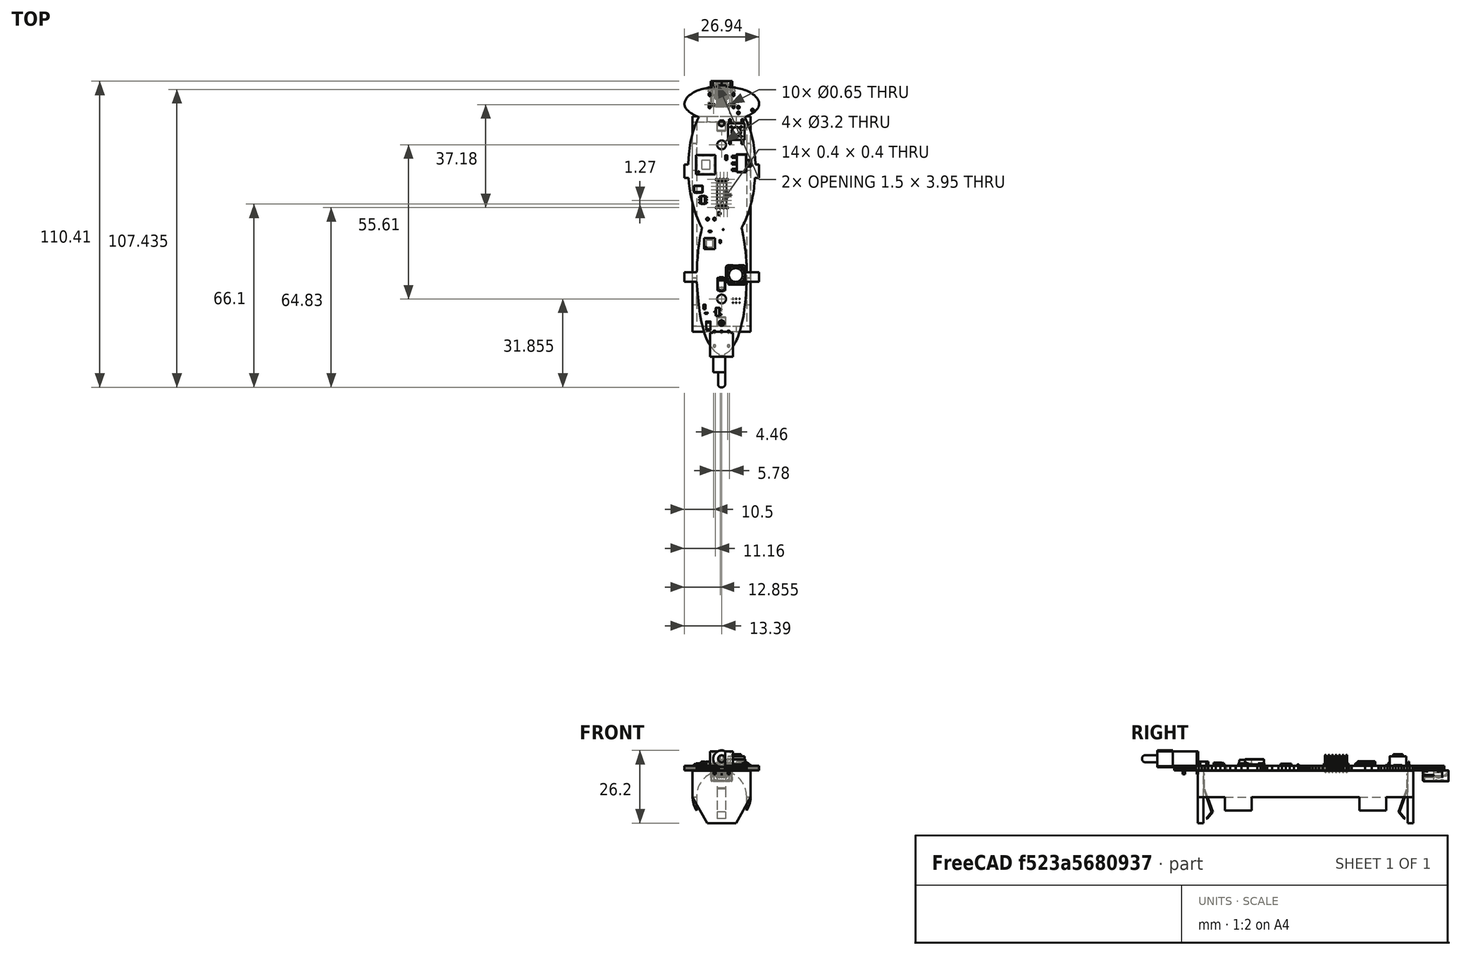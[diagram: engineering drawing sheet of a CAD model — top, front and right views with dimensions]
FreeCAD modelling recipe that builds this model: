
FCSTD DOCUMENT  (FreeCAD 0.21R30454 (Git))
Label: centerWing
License: All rights reserved
LicenseURL: http://en.wikipedia.org/wiki/All_rights_reserved
objects: App::Link×64, Part::Feature×20, App::Part×5, PartDesign::CoordinateSystem×1, Sketcher::SketchObject×1
note: 22 computed .brp shape members not serialized (recipe doc carries the construction recipe); baked Part::Feature solids carry a one-line shape summary decoded from their .brp

FEATURE [PartDesign::CoordinateSystem] Local_CS_931
  AttacherType = Attacher::AttachEngine3D
  MapMode = 2
  Support = -> [X_Axis001]
FEATURE [Part::Feature] Pcb_931
  shape: bbox 26.94 x 97.45 x 1.6 mm, 316 faces (baked)
FEATURE [Sketcher::SketchObject] PCB_Sketch_931
  FullyConstrained = false
  sketch-geometry (258):
    g0: LineSegment StartX=204.611 StartY=-59.7706 StartZ=0 EndX=204.161 EndY=-58.747 EndZ=0
    g1: LineSegment StartX=207.307 StartY=-79.6422 StartZ=0 EndX=208.849 EndY=-79.6422 EndZ=0
    g2: LineSegment StartX=203.133 StartY=-100.504 StartZ=0 EndX=202.842 EndY=-99.0355 EndZ=0
    g3: LineSegment StartX=198.204 StartY=-141.964 StartZ=0 EndX=198.335 EndY=-141.829 EndZ=0
    g4: LineSegment StartX=196.821 StartY=-46.2543 StartZ=0 EndX=195.381 EndY=-46.2543 EndZ=0
    g5: LineSegment StartX=186.994 StartY=-104.828 StartZ=0 EndX=186.849 EndY=-106.147 EndZ=0
    g6: LineSegment StartX=190.699 StartY=-139.374 StartZ=0 EndX=191.002 EndY=-139.905 EndZ=0
    g7: LineSegment StartX=194.282 StartY=-143.161 StartZ=0 EndX=194.282 EndY=-143.702 EndZ=0
    g8: LineSegment StartX=206.155 StartY=-49.1673 StartZ=0 EndX=205.642 EndY=-48.8567 EndZ=0
    g9: LineSegment StartX=207.546 StartY=-55.4632 StartZ=0 EndX=207.833 EndY=-55.1801 EndZ=0
    g10: LineSegment StartX=191.879 StartY=-141.193 StartZ=0 EndX=192.157 EndY=-141.532 EndZ=0
    g11: LineSegment StartX=186.361 StartY=-117.075 StartZ=0 EndX=186.651 EndY=-121.509 EndZ=0
    g12: LineSegment StartX=208.789 StartY=-53.5041 StartZ=0 EndX=208.834 EndY=-53.2317 EndZ=0
    g13: LineSegment StartX=206.019 StartY=-88.581 StartZ=0 EndX=206.204 EndY=-87.8001 EndZ=0
    g14: LineSegment StartX=203.931 StartY=-123.5 StartZ=0 EndX=204.11 EndY=-121.509 EndZ=0
    g15: LineSegment StartX=183.585 StartY=-81.6183 StartZ=0 EndX=183.791 EndY=-83.5056 EndZ=0
    g16: LineSegment StartX=201.902 StartY=-134.849 StartZ=0 EndX=202.197 EndY=-133.815 EndZ=0
    g17: LineSegment StartX=202.746 StartY=-97.2753 StartZ=0 EndX=202.978 EndY=-96.8717 EndZ=0
    g18: LineSegment StartX=202.76 StartY=-131.45 StartZ=0 EndX=203.025 EndY=-130.106 EndZ=0
    g19: LineSegment StartX=184.261 StartY=-65.7953 StartZ=0 EndX=184.058 EndY=-66.826 EndZ=0
    g20: LineSegment StartX=202.505 StartY=-97.6016 StartZ=0 EndX=202.585 EndY=-97.5204 EndZ=0
    g21: LineSegment StartX=196.48 StartY=-143.161 StartZ=0 EndX=196.623 EndY=-143.098 EndZ=0
    g22: LineSegment StartX=185.289 StartY=-56.8742 StartZ=0 EndX=185.841 EndY=-57.153 EndZ=0
    g23: LineSegment StartX=208.834 StartY=-53.2317 StartZ=0 EndX=208.851 EndY=-52.9624 EndZ=0
    g24: LineSegment StartX=204.4 StartY=-117.075 StartZ=0 EndX=208.849 EndY=-117.075 EndZ=0
    g25: LineSegment StartX=185.651 StartY=-48.576 StartZ=0 EndX=185.119 EndY=-48.8567 EndZ=0
    g26: LineSegment StartX=200.369 StartY=-138.788 StartZ=0 EndX=200.678 EndY=-138.143 EndZ=0
    g27: LineSegment StartX=185.964 StartY=-92.6642 StartZ=0 EndX=186.78 EndY=-94.7637 EndZ=0
    g28: LineSegment StartX=198.468 StartY=-141.686 StartZ=0 EndX=198.604 EndY=-141.532 EndZ=0
    g29: LineSegment StartX=200.262 StartY=-47.1518 StartZ=0 EndX=199.594 EndY=-47.0453 EndZ=0
    g30: LineSegment StartX=186.393 StartY=-112.527 StartZ=0 EndX=186.377 EndY=-113.724 EndZ=0
    g31: LineSegment StartX=182.209 StartY=-51.6716 StartZ=0 EndX=182.103 EndY=-51.9211 EndZ=0
    g32: LineSegment StartX=187.169 StartY=-103.429 StartZ=0 EndX=186.994 EndY=-104.828 EndZ=0
    g33: LineSegment StartX=197.156 StartY=-142.81 StartZ=0 EndX=197.366 EndY=-142.672 EndZ=0
    g34: LineSegment StartX=203.992 StartY=-48.0954 StartZ=0 EndX=203.408 EndY=-47.8915 EndZ=0
    g35: LineSegment StartX=200.678 StartY=-138.143 StartZ=0 EndX=200.987 EndY=-137.433 EndZ=0
    g36: LineSegment StartX=191.301 StartY=-140.383 StartZ=0 EndX=191.593 EndY=-140.811 EndZ=0
    g37: LineSegment StartX=186.503 StartY=-110.129 StartZ=0 EndX=186.46 EndY=-110.807 EndZ=0
    g38: LineSegment StartX=183.377 StartY=-72.3896 StartZ=0 EndX=183.215 EndY=-74.8986 EndZ=0
    g39: LineSegment StartX=206.647 StartY=-49.5098 StartZ=0 EndX=206.155 EndY=-49.1673 EndZ=0
    g40: LineSegment StartX=201.601 StartY=-135.792 StartZ=0 EndX=201.902 EndY=-134.849 EndZ=0
    g41: LineSegment StartX=203.408 StartY=-47.8915 StartZ=0 EndX=202.807 EndY=-47.709 EndZ=0
    g42: LineSegment StartX=208.428 StartY=-51.4271 StartZ=0 EndX=208.284 EndY=-51.188 EndZ=0
    g43: LineSegment StartX=182.294 StartY=-54.3351 StartZ=0 EndX=182.469 EndY=-54.6157 EndZ=0
    g44: LineSegment StartX=185.119 StartY=-48.8567 StartZ=0 EndX=184.607 EndY=-49.1673 EndZ=0
    g45: LineSegment StartX=204.382 StartY=-93.7798 StartZ=0 EndX=204.798 EndY=-92.6642 EndZ=0
    g46: LineSegment StartX=183.215 StartY=-74.8986 StartZ=0 EndX=181.912 EndY=-74.8986 EndZ=0
    g47: LineSegment StartX=205.216 StartY=-91.4223 StartZ=0 EndX=205.627 EndY=-90.0595 EndZ=0
    g48: LineSegment StartX=208.849 StartY=-74.8986 StartZ=0 EndX=207.546 EndY=-74.8986 EndZ=0
    g49: LineSegment StartX=186.651 StartY=-121.509 StartZ=0 EndX=187.031 EndY=-125.349 EndZ=0
    g50: LineSegment StartX=204.125 StartY=-108.431 StartZ=0 EndX=203.913 EndY=-106.147 EndZ=0
    g51: LineSegment StartX=187.38 StartY=-101.978 StartZ=0 EndX=187.169 EndY=-103.429 EndZ=0
    g52: LineSegment StartX=183.913 StartY=-56.0295 StartZ=0 EndX=184.326 EndY=-56.3121 EndZ=0
    g53: LineSegment StartX=205.11 StartY=-48.576 StartZ=0 EndX=204.56 EndY=-48.3229 EndZ=0
    g54: LineSegment StartX=201.561 StartY=-47.4 StartZ=0 EndX=200.918 EndY=-47.2693 EndZ=0
    g55: LineSegment StartX=204.258 StartY=-110.129 StartZ=0 EndX=204.2 EndY=-109.347 EndZ=0
    g56: LineSegment StartX=193.978 StartY=-143.02 StartZ=0 EndX=194.282 EndY=-143.161 EndZ=0
    g57: LineSegment StartX=181.958 StartY=-52.4338 StartZ=0 EndX=181.922 EndY=-52.6963 EndZ=0
    g58: LineSegment StartX=204.798 StartY=-92.6642 StartZ=0 EndX=205.216 EndY=-91.4223 EndZ=0
    g59: LineSegment StartX=204.302 StartY=-110.807 StartZ=0 EndX=204.258 EndY=-110.129 EndZ=0
    g60: LineSegment StartX=196.623 StartY=-143.098 StartZ=0 EndX=196.784 EndY=-143.02 EndZ=0
    g61: LineSegment StartX=198.227 StartY=-46.857 StartZ=0 EndX=196.821 EndY=-46.6878 EndZ=0
    g62: LineSegment StartX=204.56 StartY=-48.3229 StartZ=0 EndX=203.992 EndY=-48.0954 EndZ=0
    g63: LineSegment StartX=183.726 StartY=-68.9546 StartZ=0 EndX=183.593 EndY=-70.0623 EndZ=0
    g64: LineSegment StartX=200.215 StartY=-139.088 StartZ=0 EndX=200.369 EndY=-138.788 EndZ=0
    g65: LineSegment StartX=207.117 StartY=-49.8853 StartZ=0 EndX=206.647 EndY=-49.5098 EndZ=0
    g66: LineSegment StartX=181.972 StartY=-53.5041 StartZ=0 EndX=182.047 EndY=-53.779 EndZ=0
    g67: LineSegment StartX=184.607 StartY=-49.1673 StartZ=0 EndX=184.114 EndY=-49.5098 EndZ=0
    g68: LineSegment StartX=199.61 StartY=-140.15 StartZ=0 EndX=199.759 EndY=-139.905 EndZ=0
    g69: LineSegment StartX=205.627 StartY=-90.0595 StartZ=0 EndX=206.019 EndY=-88.581 EndZ=0
    g70: LineSegment StartX=202.679 StartY=-98.3125 StartZ=0 EndX=202.505 EndY=-97.6016 EndZ=0
    g71: LineSegment StartX=196.962 StartY=-142.925 StartZ=0 EndX=197.156 EndY=-142.81 EndZ=0
    g72: LineSegment StartX=206.204 StartY=-87.8001 StartZ=0 EndX=206.381 EndY=-86.9923 EndZ=0
    g73: LineSegment StartX=198.604 StartY=-141.532 StartZ=0 EndX=198.742 EndY=-141.368 EndZ=0
    g74: LineSegment StartX=189.774 StartY=-137.433 StartZ=0 EndX=190.393 EndY=-138.788 EndZ=0
    g75: LineSegment StartX=184.058 StartY=-66.826 StartZ=0 EndX=183.88 EndY=-67.8774 EndZ=0
    g76: LineSegment StartX=189.16 StartY=-135.792 StartZ=0 EndX=189.774 EndY=-137.433 EndZ=0
    g77: LineSegment StartX=186.151 StartY=-59.7706 StartZ=0 EndX=185.743 EndY=-60.7805 EndZ=0
    g78: LineSegment StartX=206.381 StartY=-86.9923 StartZ=0 EndX=206.547 EndY=-86.1583 EndZ=0
    g79: LineSegment StartX=208.84 StartY=-52.6963 StartZ=0 EndX=208.803 EndY=-52.4338 EndZ=0
    g80: LineSegment StartX=204.318 StartY=-57.4299 StartZ=0 EndX=204.92 EndY=-57.153 EndZ=0
    g81: LineSegment StartX=188.015 StartY=-97.2753 StartZ=0 EndX=188.257 EndY=-97.6016 EndZ=0
    g82: LineSegment StartX=205.472 StartY=-56.8742 StartZ=0 EndX=205.977 EndY=-56.5938 EndZ=0
    g83: LineSegment StartX=185.134 StartY=-90.0595 StartZ=0 EndX=185.545 EndY=-91.4223 EndZ=0
    g84: LineSegment StartX=203.512 StartY=-127.062 StartZ=0 EndX=203.731 EndY=-125.349 EndZ=0
    g85: LineSegment StartX=202.807 StartY=-47.709 StartZ=0 EndX=202.191 EndY=-47.5458 EndZ=0
    g86: LineSegment StartX=189.843 StartY=-47.2693 StartZ=0 EndX=189.2 EndY=-47.4 EndZ=0
    g87: LineSegment StartX=203.025 StartY=-130.106 StartZ=0 EndX=203.276 EndY=-128.645 EndZ=0
    g88: LineSegment StartX=199.314 StartY=-140.603 StartZ=0 EndX=199.461 EndY=-140.383 EndZ=0
    g89: LineSegment StartX=207.169 StartY=-70.0623 StartZ=0 EndX=207.035 EndY=-68.9546 EndZ=0
    g90: LineSegment StartX=199.461 StartY=-140.383 StartZ=0 EndX=199.61 EndY=-140.15 EndZ=0
    g91: LineSegment StartX=191.002 StartY=-139.905 StartZ=0 EndX=191.301 EndY=-140.383 EndZ=0
    g92: LineSegment StartX=186.46 StartY=-110.807 StartZ=0 EndX=186.429 EndY=-111.412 EndZ=0
    g93: LineSegment StartX=182.638 StartY=-50.9546 StartZ=0 EndX=182.477 EndY=-51.188 EndZ=0
    g94: LineSegment StartX=196.821 StartY=-46.6878 StartZ=0 EndX=196.821 EndY=-46.2543 EndZ=0
    g95: LineSegment StartX=183.543 StartY=-55.7465 StartZ=0 EndX=183.913 EndY=-56.0295 EndZ=0
    g96: LineSegment StartX=181.912 StartY=-117.075 StartZ=0 EndX=186.361 EndY=-117.075 EndZ=0
    g97: LineSegment StartX=204.2 StartY=-109.347 StartZ=0 EndX=204.125 EndY=-108.431 EndZ=0
    g98: LineSegment StartX=181.911 StartY=-52.9624 StartZ=0 EndX=181.927 EndY=-53.2317 EndZ=0
    g99: LineSegment StartX=206.702 StartY=-85.2987 StartZ=0 EndX=206.844 EndY=-84.4142 EndZ=0
    g100: LineSegment StartX=208.742 StartY=-52.1753 StartZ=0 EndX=208.658 EndY=-51.9211 EndZ=0
    g101: LineSegment StartX=192.686 StartY=-142.089 StartZ=0 EndX=192.935 EndY=-142.314 EndZ=0
    g102: LineSegment StartX=187.095 StartY=-57.7046 StartZ=0 EndX=186.6 EndY=-58.747 EndZ=0
    g103: LineSegment StartX=208.849 StartY=-117.075 StartZ=0 EndX=208.849 EndY=-113.724 EndZ=0
    g104: LineSegment StartX=196.784 StartY=-143.02 StartZ=0 EndX=196.962 EndY=-142.925 EndZ=0
    g105: LineSegment StartX=186.6 StartY=-58.747 StartZ=0 EndX=186.151 EndY=-59.7706 EndZ=0
    g106: LineSegment StartX=184.785 StartY=-56.5938 StartZ=0 EndX=185.289 EndY=-56.8742 EndZ=0
    g107: LineSegment StartX=198.882 StartY=-141.193 StartZ=0 EndX=199.024 EndY=-141.008 EndZ=0
    g108: LineSegment StartX=191.167 StartY=-47.0453 StartZ=0 EndX=189.843 EndY=-47.2693 EndZ=0
    g109: LineSegment StartX=182.103 StartY=-51.9211 StartZ=0 EndX=182.019 EndY=-52.1753 EndZ=0
    g110: LineSegment StartX=200.918 StartY=-47.2693 StartZ=0 EndX=200.262 EndY=-47.1518 EndZ=0
    g111: LineSegment StartX=203.268 StartY=-96.315 StartZ=0 EndX=203.607 EndY=-95.6105 EndZ=0
    g112: LineSegment StartX=188.565 StartY=-133.815 StartZ=0 EndX=189.16 EndY=-135.792 EndZ=0
    g113: LineSegment StartX=207.218 StartY=-55.7465 StartZ=0 EndX=207.546 EndY=-55.4632 EndZ=0
    g114: LineSegment StartX=207.252 StartY=-80.641 StartZ=0 EndX=207.307 EndY=-79.6422 EndZ=0
    g115: LineSegment StartX=188.257 StartY=-97.6016 StartZ=0 EndX=187.92 EndY=-99.0355 EndZ=0
    g116: LineSegment StartX=186.443 StartY=-57.4299 StartZ=0 EndX=187.095 EndY=-57.7046 EndZ=0
    g117: LineSegment StartX=203.607 StartY=-95.6105 StartZ=0 EndX=203.982 EndY=-94.7637 EndZ=0
    g118: LineSegment StartX=207.554 StartY=-50.2921 StartZ=0 EndX=207.117 EndY=-49.8853 EndZ=0
    g119: LineSegment StartX=185.841 StartY=-57.153 StartZ=0 EndX=186.443 EndY=-57.4299 EndZ=0
    g120: LineSegment StartX=204.267 StartY=-119.37 StartZ=0 EndX=204.4 EndY=-117.075 EndZ=0
    g121: LineSegment StartX=199.168 StartY=-140.811 StartZ=0 EndX=199.314 EndY=-140.603 EndZ=0
    g122: LineSegment StartX=199.91 StartY=-139.646 StartZ=0 EndX=200.062 EndY=-139.374 EndZ=0
    g123: LineSegment StartX=203.731 StartY=-125.349 StartZ=0 EndX=203.931 EndY=-123.5 EndZ=0
    g124: LineSegment StartX=206.844 StartY=-84.4142 StartZ=0 EndX=206.971 EndY=-83.5056 EndZ=0
    g125: LineSegment StartX=203.913 StartY=-106.147 StartZ=0 EndX=203.768 EndY=-104.828 EndZ=0
    g126: LineSegment StartX=206.848 StartY=-56.0295 StartZ=0 EndX=207.218 EndY=-55.7465 EndZ=0
    g127: LineSegment StartX=198.335 StartY=-141.829 StartZ=0 EndX=198.468 EndY=-141.686 EndZ=0
    g128: LineSegment StartX=204.333 StartY=-111.412 StartZ=0 EndX=204.302 EndY=-110.807 EndZ=0
    g129: LineSegment StartX=183.004 StartY=-50.5063 StartZ=0 EndX=182.814 EndY=-50.7272 EndZ=0
    g130: LineSegment StartX=183.88 StartY=-67.8774 StartZ=0 EndX=183.726 EndY=-68.9546 EndZ=0
    g131: LineSegment StartX=181.912 StartY=-79.6422 StartZ=0 EndX=183.454 EndY=-79.6422 EndZ=0
    g132: LineSegment StartX=198.075 StartY=-142.089 StartZ=0 EndX=198.204 EndY=-141.964 EndZ=0
    g133: LineSegment StartX=200.062 StartY=-139.374 StartZ=0 EndX=200.215 EndY=-139.088 EndZ=0
    g134: LineSegment StartX=185.545 StartY=-91.4223 StartZ=0 EndX=185.964 EndY=-92.6642 EndZ=0
    g135: LineSegment StartX=202.978 StartY=-96.8717 StartZ=0 EndX=203.268 EndY=-96.315 EndZ=0
    g136: LineSegment StartX=205.018 StartY=-60.7805 StartZ=0 EndX=204.611 EndY=-59.7706 EndZ=0
    g137: LineSegment StartX=187.954 StartY=-47.709 StartZ=0 EndX=187.354 EndY=-47.8915 EndZ=0
    g138: LineSegment StartX=208.292 StartY=-54.6157 StartZ=0 EndX=208.467 EndY=-54.3351 EndZ=0
    g139: LineSegment StartX=187.92 StartY=-99.0355 StartZ=0 EndX=187.629 EndY=-100.504 EndZ=0
    g140: LineSegment StartX=208.658 StartY=-51.9211 StartZ=0 EndX=208.553 EndY=-51.6716 EndZ=0
    g141: LineSegment StartX=188.002 StartY=-131.45 StartZ=0 EndX=188.565 EndY=-133.815 EndZ=0
    g142: LineSegment StartX=204.11 StartY=-121.509 StartZ=0 EndX=204.267 EndY=-119.37 EndZ=0
    g143: LineSegment StartX=196.48 StartY=-143.702 StartZ=0 EndX=196.48 EndY=-143.161 EndZ=0
    g144: LineSegment StartX=183.791 StartY=-83.5056 StartZ=0 EndX=184.059 EndY=-85.2987 EndZ=0
    g145: LineSegment StartX=193.605 StartY=-142.81 StartZ=0 EndX=193.8 EndY=-142.925 EndZ=0
    g146: LineSegment StartX=186.636 StartY=-108.431 StartZ=0 EndX=186.503 EndY=-110.129 EndZ=0
    g147: LineSegment StartX=192.535 StartY=-46.857 StartZ=0 EndX=191.167 EndY=-47.0453 EndZ=0
    g148: LineSegment StartX=198.742 StartY=-141.368 StartZ=0 EndX=198.882 EndY=-141.193 EndZ=0
    g149: LineSegment StartX=182.814 StartY=-50.7272 StartZ=0 EndX=182.638 EndY=-50.9546 EndZ=0
    g150: LineSegment StartX=187.031 StartY=-125.349 StartZ=0 EndX=187.486 EndY=-128.645 EndZ=0
    g151: LineSegment StartX=183.421 StartY=-50.085 StartZ=0 EndX=183.207 EndY=-50.2921 EndZ=0
    g152: LineSegment StartX=204.368 StartY=-112.527 StartZ=0 EndX=204.354 EndY=-111.975 EndZ=0
    g153: LineSegment StartX=202.585 StartY=-97.5204 StartZ=0 EndX=202.746 EndY=-97.2753 EndZ=0
    g154: LineSegment StartX=184.742 StartY=-88.581 StartZ=0 EndX=185.134 EndY=-90.0595 EndZ=0
    g155: LineSegment StartX=183.454 StartY=-79.6422 StartZ=0 EndX=183.585 EndY=-81.6183 EndZ=0
    g156: LineSegment StartX=206.971 StartY=-83.5056 StartZ=0 EndX=207.082 EndY=-82.5734 EndZ=0
    g157: LineSegment StartX=206.704 StartY=-66.826 StartZ=0 EndX=206.501 EndY=-65.7953 EndZ=0
    g158: LineSegment StartX=203.592 StartY=-103.429 StartZ=0 EndX=203.382 EndY=-101.978 EndZ=0
    g159: LineSegment StartX=208.714 StartY=-53.779 StartZ=0 EndX=208.789 EndY=-53.5041 EndZ=0
    g160: LineSegment StartX=203.276 StartY=-128.645 StartZ=0 EndX=203.512 EndY=-127.062 EndZ=0
    g161: LineSegment StartX=186.429 StartY=-111.412 StartZ=0 EndX=186.393 EndY=-112.527 EndZ=0
    g162: LineSegment StartX=197.826 StartY=-142.314 StartZ=0 EndX=198.075 EndY=-142.089 EndZ=0
    g163: LineSegment StartX=193.396 StartY=-142.672 StartZ=0 EndX=193.605 EndY=-142.81 EndZ=0
    g164: LineSegment StartX=208.851 StartY=-52.9624 StartZ=0 EndX=208.84 EndY=-52.6963 EndZ=0
    g165: LineSegment StartX=197.59 StartY=-142.507 StartZ=0 EndX=197.826 EndY=-142.314 EndZ=0
    g166: LineSegment StartX=206.009 StartY=-63.7765 StartZ=0 EndX=205.715 EndY=-62.7784 EndZ=0
    g167: LineSegment StartX=185.743 StartY=-60.7805 StartZ=0 EndX=185.376 EndY=-61.7814 EndZ=0
    g168: LineSegment StartX=195.381 StartY=-143.702 StartZ=0 EndX=196.48 EndY=-143.702 EndZ=0
    g169: LineSegment StartX=183.593 StartY=-70.0623 StartZ=0 EndX=183.377 EndY=-72.3896 EndZ=0
    g170: LineSegment StartX=206.501 StartY=-65.7953 StartZ=0 EndX=206.27 EndY=-64.7804 EndZ=0
    g171: LineSegment StartX=200.987 StartY=-137.433 StartZ=0 EndX=201.296 EndY=-136.651 EndZ=0
    g172: LineSegment StartX=191.593 StartY=-140.811 StartZ=0 EndX=191.879 EndY=-141.193 EndZ=0
    g173: LineSegment StartX=182.154 StartY=-54.0561 StartZ=0 EndX=182.294 EndY=-54.3351 EndZ=0
    g174: LineSegment StartX=208.607 StartY=-54.0561 StartZ=0 EndX=208.714 EndY=-53.779 EndZ=0
    g175: LineSegment StartX=182.047 StartY=-53.779 StartZ=0 EndX=182.154 EndY=-54.0561 EndZ=0
    g176: LineSegment StartX=199.024 StartY=-141.008 StartZ=0 EndX=199.168 EndY=-140.811 EndZ=0
    g177: LineSegment StartX=192.935 StartY=-142.314 StartZ=0 EndX=193.172 EndY=-142.507 EndZ=0
    g178: LineSegment StartX=189.2 StartY=-47.4 StartZ=0 EndX=188.57 EndY=-47.5458 EndZ=0
    g179: LineSegment StartX=182.68 StartY=-54.8975 StartZ=0 EndX=182.928 EndY=-55.1801 EndZ=0
    g180: LineSegment StartX=186.377 StartY=-113.724 StartZ=0 EndX=181.912 EndY=-113.724 EndZ=0
    g181: LineSegment StartX=202.483 StartY=-132.685 StartZ=0 EndX=202.76 EndY=-131.45 EndZ=0
    g182: LineSegment StartX=183.216 StartY=-55.4632 StartZ=0 EndX=183.543 EndY=-55.7465 EndZ=0
    g183: LineSegment StartX=206.435 StartY=-56.3121 StartZ=0 EndX=206.848 EndY=-56.0295 EndZ=0
    g184: LineSegment StartX=184.326 StartY=-56.3121 StartZ=0 EndX=184.785 EndY=-56.5938 EndZ=0
    g185: LineSegment StartX=184.753 StartY=-63.7765 StartZ=0 EndX=184.492 EndY=-64.7804 EndZ=0
    g186: LineSegment StartX=206.27 StartY=-64.7804 StartZ=0 EndX=206.009 EndY=-63.7765 EndZ=0
    g187: LineSegment StartX=186.202 StartY=-48.3229 StartZ=0 EndX=185.651 EndY=-48.576 EndZ=0
    g188: LineSegment StartX=205.385 StartY=-61.7814 StartZ=0 EndX=205.018 EndY=-60.7805 EndZ=0
    g189: LineSegment StartX=208.467 StartY=-54.3351 StartZ=0 EndX=208.607 EndY=-54.0561 EndZ=0
    g190: LineSegment StartX=187.629 StartY=-100.504 StartZ=0 EndX=187.38 EndY=-101.978 EndZ=0
    g191: LineSegment StartX=207.176 StartY=-81.6183 StartZ=0 EndX=207.252 EndY=-80.641 EndZ=0
    g192: LineSegment StartX=208.082 StartY=-54.8975 StartZ=0 EndX=208.292 EndY=-54.6157 EndZ=0
    g193: LineSegment StartX=204.385 StartY=-113.724 StartZ=0 EndX=204.368 EndY=-112.527 EndZ=0
    g194: LineSegment StartX=208.849 StartY=-113.724 StartZ=0 EndX=204.385 EndY=-113.724 EndZ=0
    g195: LineSegment StartX=201.296 StartY=-136.651 StartZ=0 EndX=201.601 EndY=-135.792 EndZ=0
    g196: LineSegment StartX=183.207 StartY=-50.2921 StartZ=0 EndX=183.004 EndY=-50.5063 EndZ=0
    g197: LineSegment StartX=188.57 StartY=-47.5458 StartZ=0 EndX=187.954 EndY=-47.709 EndZ=0
    g198: LineSegment StartX=190.393 StartY=-138.788 StartZ=0 EndX=190.699 EndY=-139.374 EndZ=0
    g199: LineSegment StartX=185.047 StartY=-62.7784 StartZ=0 EndX=184.753 EndY=-63.7765 EndZ=0
    g200: LineSegment StartX=199.594 StartY=-47.0453 StartZ=0 EndX=198.227 EndY=-46.857 EndZ=0
    g201: LineSegment StartX=204.92 StartY=-57.153 StartZ=0 EndX=205.472 EndY=-56.8742 EndZ=0
    g202: LineSegment StartX=207.546 StartY=-74.8986 StartZ=0 EndX=207.384 EndY=-72.3896 EndZ=0
    g203: LineSegment StartX=208.849 StartY=-79.6422 StartZ=0 EndX=208.849 EndY=-74.8986 EndZ=0
    g204: LineSegment StartX=203.382 StartY=-101.978 StartZ=0 EndX=203.133 EndY=-100.504 EndZ=0
    g205: LineSegment StartX=205.977 StartY=-56.5938 StartZ=0 EndX=206.435 EndY=-56.3121 EndZ=0
    g206: LineSegment StartX=185.376 StartY=-61.7814 StartZ=0 EndX=185.047 EndY=-62.7784 EndZ=0
    g207: LineSegment StartX=184.38 StartY=-86.9923 StartZ=0 EndX=184.742 EndY=-88.581 EndZ=0
    g208: LineSegment StartX=193.8 StartY=-142.925 StartZ=0 EndX=193.978 EndY=-143.02 EndZ=0
    g209: LineSegment StartX=181.912 StartY=-74.8986 StartZ=0 EndX=181.912 EndY=-79.6422 EndZ=0
    g210: LineSegment StartX=182.334 StartY=-51.4271 StartZ=0 EndX=182.209 EndY=-51.6716 EndZ=0
    g211: LineSegment StartX=195.381 StartY=-46.2543 StartZ=0 EndX=193.94 EndY=-46.2543 EndZ=0
    g212: LineSegment StartX=181.922 StartY=-52.6963 StartZ=0 EndX=181.911 EndY=-52.9624 EndZ=0
    g213: LineSegment StartX=192.427 StartY=-141.829 StartZ=0 EndX=192.686 EndY=-142.089 EndZ=0
    g214: LineSegment StartX=208.284 StartY=-51.188 StartZ=0 EndX=208.123 EndY=-50.9546 EndZ=0
    g215: LineSegment StartX=186.769 StartY=-48.0954 StartZ=0 EndX=186.202 EndY=-48.3229 EndZ=0
    g216: LineSegment StartX=202.191 StartY=-47.5458 StartZ=0 EndX=201.561 EndY=-47.4 EndZ=0
    g217: LineSegment StartX=183.644 StartY=-49.8853 StartZ=0 EndX=183.421 EndY=-50.085 EndZ=0
    g218: LineSegment StartX=187.354 StartY=-47.8915 StartZ=0 EndX=186.769 EndY=-48.0954 EndZ=0
    g219: LineSegment StartX=197.366 StartY=-142.672 StartZ=0 EndX=197.59 EndY=-142.507 EndZ=0
    g220: LineSegment StartX=207.947 StartY=-50.7272 StartZ=0 EndX=207.554 EndY=-50.2921 EndZ=0
    g221: LineSegment StartX=187.493 StartY=-96.315 StartZ=0 EndX=188.015 EndY=-97.2753 EndZ=0
    g222: LineSegment StartX=192.157 StartY=-141.532 StartZ=0 EndX=192.427 EndY=-141.829 EndZ=0
    g223: LineSegment StartX=184.059 StartY=-85.2987 StartZ=0 EndX=184.38 EndY=-86.9923 EndZ=0
    g224: LineSegment StartX=181.927 StartY=-53.2317 StartZ=0 EndX=181.972 EndY=-53.5041 EndZ=0
    g225: LineSegment StartX=202.197 StartY=-133.815 StartZ=0 EndX=202.483 EndY=-132.685 EndZ=0
    g226: LineSegment StartX=194.282 StartY=-143.702 StartZ=0 EndX=195.381 EndY=-143.702 EndZ=0
    g227: LineSegment StartX=203.982 StartY=-94.7637 StartZ=0 EndX=204.382 EndY=-93.7798 EndZ=0
    g228: LineSegment StartX=184.492 StartY=-64.7804 StartZ=0 EndX=184.261 EndY=-65.7953 EndZ=0
    g229: LineSegment StartX=193.172 StartY=-142.507 StartZ=0 EndX=193.396 EndY=-142.672 EndZ=0
    g230: LineSegment StartX=182.928 StartY=-55.1801 StartZ=0 EndX=183.216 EndY=-55.4632 EndZ=0
    g231: LineSegment StartX=204.161 StartY=-58.747 StartZ=0 EndX=203.666 EndY=-57.7046 EndZ=0
    g232: LineSegment StartX=182.477 StartY=-51.188 StartZ=0 EndX=182.334 EndY=-51.4271 EndZ=0
    g233: LineSegment StartX=199.759 StartY=-139.905 StartZ=0 EndX=199.91 EndY=-139.646 EndZ=0
    g234: LineSegment StartX=187.486 StartY=-128.645 StartZ=0 EndX=188.002 EndY=-131.45 EndZ=0
    g235: LineSegment StartX=205.642 StartY=-48.8567 StartZ=0 EndX=205.11 EndY=-48.576 EndZ=0
    g236: LineSegment StartX=207.035 StartY=-68.9546 StartZ=0 EndX=206.881 EndY=-67.8774 EndZ=0
    g237: LineSegment StartX=181.912 StartY=-113.724 StartZ=0 EndX=181.912 EndY=-117.075 EndZ=0
    g238: LineSegment StartX=208.553 StartY=-51.6716 StartZ=0 EndX=208.428 EndY=-51.4271 EndZ=0
    g239: LineSegment StartX=202.842 StartY=-99.0355 StartZ=0 EndX=202.679 EndY=-98.3125 EndZ=0
    g240: LineSegment StartX=207.384 StartY=-72.3896 StartZ=0 EndX=207.169 EndY=-70.0623 EndZ=0
    g241: LineSegment StartX=186.849 StartY=-106.147 StartZ=0 EndX=186.636 EndY=-108.431 EndZ=0
    g242: LineSegment StartX=208.803 StartY=-52.4338 StartZ=0 EndX=208.742 EndY=-52.1753 EndZ=0
    g243: LineSegment StartX=182.469 StartY=-54.6157 StartZ=0 EndX=182.68 EndY=-54.8975 EndZ=0
    g244: LineSegment StartX=182.019 StartY=-52.1753 StartZ=0 EndX=181.958 EndY=-52.4338 EndZ=0
    g245: LineSegment StartX=203.768 StartY=-104.828 StartZ=0 EndX=203.592 EndY=-103.429 EndZ=0
    g246: LineSegment StartX=206.547 StartY=-86.1583 StartZ=0 EndX=206.702 EndY=-85.2987 EndZ=0
    g247: LineSegment StartX=207.082 StartY=-82.5734 StartZ=0 EndX=207.176 EndY=-81.6183 EndZ=0
    g248: LineSegment StartX=184.114 StartY=-49.5098 StartZ=0 EndX=183.644 EndY=-49.8853 EndZ=0
    g249: LineSegment StartX=207.833 StartY=-55.1801 StartZ=0 EndX=208.082 EndY=-54.8975 EndZ=0
    g250: LineSegment StartX=193.94 StartY=-46.2543 StartZ=0 EndX=193.94 EndY=-46.6878 EndZ=0
    g251: LineSegment StartX=206.881 StartY=-67.8774 StartZ=0 EndX=206.704 EndY=-66.826 EndZ=0
    g252: LineSegment StartX=186.78 StartY=-94.7637 StartZ=0 EndX=187.493 EndY=-96.315 EndZ=0
    g253: LineSegment StartX=204.354 StartY=-111.975 StartZ=0 EndX=204.333 EndY=-111.412 EndZ=0
    g254: LineSegment StartX=203.666 StartY=-57.7046 StartZ=0 EndX=204.318 EndY=-57.4299 EndZ=0
    g255: LineSegment StartX=208.123 StartY=-50.9546 StartZ=0 EndX=207.947 EndY=-50.7272 EndZ=0
    g256: LineSegment StartX=205.715 StartY=-62.7784 StartZ=0 EndX=205.385 EndY=-61.7814 EndZ=0
    g257: LineSegment StartX=193.94 StartY=-46.6878 StartZ=0 EndX=192.535 EndY=-46.857 EndZ=0
  constraints (258):
    c: Coincident(g96,g237)
    c: Coincident(g180,g237)
    c: Coincident(g131,g209)
    c: Coincident(g46,g209)
    c: Coincident(g98,g212)
    c: Coincident(g98,g224)
    c: Coincident(g57,g212)
    c: Coincident(g57,g244)
    c: Coincident(g66,g224)
    c: Coincident(g109,g244)
    c: Coincident(g66,g175)
    c: Coincident(g31,g109)
    c: Coincident(g173,g175)
    c: Coincident(g31,g210)
    c: Coincident(g43,g173)
    c: Coincident(g210,g232)
    c: Coincident(g43,g243)
    c: Coincident(g93,g232)
    c: Coincident(g93,g149)
    c: Coincident(g179,g243)
    c: Coincident(g129,g149)
    c: Coincident(g179,g230)
    c: Coincident(g129,g196)
    c: Coincident(g38,g46)
    c: Coincident(g182,g230)
    c: Coincident(g151,g196)
    c: Coincident(g38,g169)
    c: Coincident(g151,g217)
    c: Coincident(g131,g155)
    c: Coincident(g95,g182)
    c: Coincident(g15,g155)
    c: Coincident(g63,g169)
    c: Coincident(g217,g248)
    c: Coincident(g63,g130)
    c: Coincident(g15,g144)
    c: Coincident(g75,g130)
    c: Coincident(g52,g95)
    c: Coincident(g144,g223)
    c: Coincident(g19,g75)
    c: Coincident(g67,g248)
    c: Coincident(g19,g228)
    c: Coincident(g52,g184)
    c: Coincident(g207,g223)
    c: Coincident(g185,g228)
    c: Coincident(g44,g67)
    c: Coincident(g154,g207)
    c: Coincident(g185,g199)
    c: Coincident(g106,g184)
    c: Coincident(g199,g206)
    c: Coincident(g25,g44)
    c: Coincident(g83,g154)
    c: Coincident(g22,g106)
    c: Coincident(g167,g206)
    c: Coincident(g83,g134)
    c: Coincident(g25,g187)
    c: Coincident(g77,g167)
    c: Coincident(g22,g119)
    c: Coincident(g27,g134)
    c: Coincident(g77,g105)
    c: Coincident(g187,g215)
    c: Coincident(g11,g96)
    c: Coincident(g30,g180)
    c: Coincident(g30,g161)
    c: Coincident(g92,g161)
    c: Coincident(g116,g119)
    c: Coincident(g37,g92)
    c: Coincident(g37,g146)
    c: Coincident(g102,g105)
    c: Coincident(g146,g241)
    c: Coincident(g11,g49)
    c: Coincident(g215,g218)
    c: Coincident(g27,g252)
    c: Coincident(g5,g241)
    c: Coincident(g5,g32)
    c: Coincident(g49,g150)
    c: Coincident(g102,g116)
    c: Coincident(g32,g51)
    c: Coincident(g137,g218)
    c: Coincident(g51,g190)
    c: Coincident(g150,g234)
    c: Coincident(g221,g252)
    c: Coincident(g139,g190)
    c: Coincident(g115,g139)
    c: Coincident(g137,g197)
    c: Coincident(g141,g234)
    c: Coincident(g81,g221)
    c: Coincident(g81,g115)
    c: Coincident(g112,g141)
    c: Coincident(g178,g197)
    c: Coincident(g76,g112)
    c: Coincident(g86,g178)
    c: Coincident(g74,g76)
    c: Coincident(g86,g108)
    c: Coincident(g74,g198)
    c: Coincident(g6,g198)
    c: Coincident(g6,g91)
    c: Coincident(g108,g147)
    c: Coincident(g36,g91)
    c: Coincident(g36,g172)
    c: Coincident(g10,g172)
    c: Coincident(g10,g222)
    c: Coincident(g213,g222)
    c: Coincident(g147,g257)
    c: Coincident(g101,g213)
    c: Coincident(g101,g177)
    c: Coincident(g177,g229)
    c: Coincident(g163,g229)
    c: Coincident(g145,g163)
    c: Coincident(g145,g208)
    c: Coincident(g250,g257)
    c: Coincident(g211,g250)
    c: Coincident(g56,g208)
    c: Coincident(g7,g226)
    c: Coincident(g7,g56)
    c: Coincident(g168,g226)
    c: Coincident(g4,g211)
    c: Coincident(g143,g168)
    c: Coincident(g21,g143)
    c: Coincident(g21,g60)
    c: Coincident(g60,g104)
    c: Coincident(g61,g94)
    c: Coincident(g4,g94)
    c: Coincident(g71,g104)
    c: Coincident(g33,g71)
    c: Coincident(g33,g219)
    c: Coincident(g165,g219)
    c: Coincident(g162,g165)
    c: Coincident(g132,g162)
    c: Coincident(g3,g132)
    c: Coincident(g61,g200)
    c: Coincident(g3,g127)
    c: Coincident(g28,g127)
    c: Coincident(g28,g73)
    c: Coincident(g73,g148)
    c: Coincident(g107,g148)
    c: Coincident(g107,g176)
    c: Coincident(g121,g176)
    c: Coincident(g88,g121)
    c: Coincident(g88,g90)
    c: Coincident(g29,g200)
    c: Coincident(g68,g90)
    c: Coincident(g68,g233)
    c: Coincident(g122,g233)
    c: Coincident(g122,g133)
    c: Coincident(g64,g133)
    c: Coincident(g29,g110)
    c: Coincident(g26,g64)
    c: Coincident(g26,g35)
    c: Coincident(g54,g110)
    c: Coincident(g35,g171)
    c: Coincident(g171,g195)
    c: Coincident(g54,g216)
    c: Coincident(g40,g195)
    c: Coincident(g16,g40)
    c: Coincident(g16,g225)
    c: Coincident(g85,g216)
    c: Coincident(g181,g225)
    c: Coincident(g20,g70)
    c: Coincident(g20,g153)
    c: Coincident(g70,g239)
    c: Coincident(g17,g153)
    c: Coincident(g18,g181)
    c: Coincident(g41,g85)
    c: Coincident(g2,g239)
    c: Coincident(g17,g135)
    c: Coincident(g18,g87)
    c: Coincident(g2,g204)
    c: Coincident(g87,g160)
    c: Coincident(g111,g135)
    c: Coincident(g158,g204)
    c: Coincident(g34,g41)
    c: Coincident(g84,g160)
    c: Coincident(g158,g245)
    c: Coincident(g111,g117)
    c: Coincident(g231,g254)
    c: Coincident(g84,g123)
    c: Coincident(g125,g245)
    c: Coincident(g50,g125)
    c: Coincident(g14,g123)
    c: Coincident(g117,g227)
    c: Coincident(g34,g62)
    c: Coincident(g14,g142)
    c: Coincident(g50,g97)
    c: Coincident(g0,g231)
    c: Coincident(g55,g97)
    c: Coincident(g120,g142)
    c: Coincident(g55,g59)
    c: Coincident(g59,g128)
    c: Coincident(g80,g254)
    c: Coincident(g128,g253)
    c: Coincident(g152,g253)
    c: Coincident(g152,g193)
    c: Coincident(g193,g194)
    c: Coincident(g45,g227)
    c: Coincident(g24,g120)
    c: Coincident(g53,g62)
    c: Coincident(g0,g136)
    c: Coincident(g45,g58)
    c: Coincident(g80,g201)
    c: Coincident(g136,g188)
    c: Coincident(g53,g235)
    c: Coincident(g47,g58)
    c: Coincident(g188,g256)
    c: Coincident(g82,g201)
    c: Coincident(g47,g69)
    c: Coincident(g8,g235)
    c: Coincident(g166,g256)
    c: Coincident(g82,g205)
    c: Coincident(g166,g186)
    c: Coincident(g13,g69)
    c: Coincident(g8,g39)
    c: Coincident(g13,g72)
    c: Coincident(g170,g186)
    c: Coincident(g72,g78)
    c: Coincident(g183,g205)
    c: Coincident(g157,g170)
    c: Coincident(g78,g246)
    c: Coincident(g39,g65)
    c: Coincident(g99,g246)
    c: Coincident(g157,g251)
    c: Coincident(g99,g124)
    c: Coincident(g126,g183)
    c: Coincident(g236,g251)
    c: Coincident(g124,g156)
    c: Coincident(g89,g236)
    c: Coincident(g156,g247)
    c: Coincident(g65,g118)
    c: Coincident(g191,g247)
    c: Coincident(g89,g240)
    c: Coincident(g113,g126)
    c: Coincident(g114,g191)
    c: Coincident(g1,g114)
    c: Coincident(g202,g240)
    c: Coincident(g48,g202)
    c: Coincident(g9,g113)
    c: Coincident(g118,g220)
    c: Coincident(g9,g249)
    c: Coincident(g220,g255)
    c: Coincident(g192,g249)
    c: Coincident(g214,g255)
    c: Coincident(g138,g192)
    c: Coincident(g42,g214)
    c: Coincident(g42,g238)
    c: Coincident(g138,g189)
    c: Coincident(g140,g238)
    c: Coincident(g174,g189)
    c: Coincident(g100,g140)
    c: Coincident(g159,g174)
    c: Coincident(g100,g242)
    c: Coincident(g12,g159)
    c: Coincident(g79,g242)
    c: Coincident(g12,g23)
    c: Coincident(g24,g103)
    c: Coincident(g103,g194)
    c: Coincident(g1,g203)
    c: Coincident(g48,g203)
    c: Coincident(g79,g164)
    c: Coincident(g23,g164)
FEATURE [App::Part] Board_Geoms_931
  Group = -> [Pcb_931,PCB_Sketch_931]
  Origin = -> Origin
FEATURE [Part::Feature] Shape  label="R21_C_0402_1005Metric_38c94f1f1ba7"
  Placement = pos=(189.8,-128.5,0) rot=(0,0,1;3.14159rad)
  shape: bbox 1 x 0.5 x 0.5 mm, 28 faces (baked)
FEATURE [App::Link] R21_C_0402_1005Metric_38c94f1f1ba7_ln_  label="R20_C_0402_1005Metric_7b8d80ad2dcc"
  LinkPlacement = pos=(189.9,-114.1,0) rot=(0,0,1;3.14159rad)
  LinkedObject = -> Shape
  Placement = pos=(189.9,-114.1,0) rot=(0,0,1;3.14159rad)
FEATURE [App::Link] R21_C_0402_1005Metric_38c94f1f1ba7_ln_001  label="C1_C_0402_1005Metric_d29c508b4b60"
  LinkPlacement = pos=(195.2,-70.7,0) rot=(0,0,1;0rad)
  LinkedObject = -> Shape
  Placement = pos=(195.2,-70.7,0) rot=(0,0,1;0rad)
FEATURE [Part::Feature] Shape001  label="R19_R_0402_1005Metric_9ca80ee487fc"
  Placement = pos=(194.8,-102.6,0) rot=(0,0,-1;1.5708rad)
  shape: bbox 0.5 x 1 x 0.35 mm, 26 faces (baked)
FEATURE [App::Link] R21_C_0402_1005Metric_38c94f1f1ba7_ln_002  label="C9_C_0402_1005Metric_a875c5e367f2"
  LinkPlacement = pos=(190.3,-80.1,0) rot=(0,0,-1;1.5708rad)
  LinkedObject = -> Shape
  Placement = pos=(190.3,-80.1,0) rot=(0,0,-1;1.5708rad)
FEATURE [Part::Feature] Shape002  label="D2_D_SMA_34cf3897dfc1"
  Placement = pos=(195.2,-118,0) rot=(0,0,-1;1.5708rad)
  shape: bbox 2.7 x 5 x 2.22 mm, 41 faces (baked)
FEATURE [Part::Feature] Shape003  label="C42_C_0603_1608Metric_3f0e18eb3bdb"
  Placement = pos=(197,-72.4,0) rot=(0,0,1;1.5708rad)
  shape: bbox 0.8 x 1.6 x 0.8 mm, 28 faces (baked)
FEATURE [Part::Feature] Shape004  label="SW3_Fillet_54ad2342c7e7"
  Placement = pos=(195.3,-140.21,0) rot=(0,0,1;3.14159rad)
  shape: bbox 8.3 x 20.48 x 8.6 mm, 32 faces (baked)
FEATURE [Part::Feature] Shape005  label="U5_SOT_223_0bc22c24d438"
  Placement = pos=(202.5,-74.4,0) rot=(0,0,1;0rad)
  shape: bbox 7 x 6.5 x 1.7 mm, 78 faces (baked)
FEATURE [App::Link] R19_R_0402_1005Metric_9ca80ee487fc_ln_  label="R2_R_0402_1005Metric_dea8e135976e"
  LinkPlacement = pos=(201.5,-68.7,0) rot=(0,0,1;1.5708rad)
  LinkedObject = -> Shape001
  Placement = pos=(201.5,-68.7,0) rot=(0,0,1;1.5708rad)
FEATURE [App::Link] C42_C_0603_1608Metric_3f0e18eb3bdb_ln_  label="C45_C_0603_1608Metric_d322fa890f2c"
  LinkPlacement = pos=(188.9,-123.4,0) rot=(0,0,1;0rad)
  LinkedObject = -> Shape003
  Placement = pos=(188.9,-123.4,0) rot=(0,0,1;0rad)
FEATURE [App::Link] R21_C_0402_1005Metric_38c94f1f1ba7_ln_003  label="C46_C_0402_1005Metric_a9bfb0d6892e"
  LinkPlacement = pos=(189.1,-100.1,0) rot=(0,0,1;0rad)
  LinkedObject = -> Shape
  Placement = pos=(189.1,-100.1,0) rot=(0,0,1;0rad)
FEATURE [App::Link] R19_R_0402_1005Metric_9ca80ee487fc_ln_001  label="R15_R_0402_1005Metric_e6cf502f8789"
  LinkPlacement = pos=(187.7,-106.9,0) rot=(0,0,-1;1.5708rad)
  LinkedObject = -> Shape001
  Placement = pos=(187.7,-106.9,0) rot=(0,0,-1;1.5708rad)
FEATURE [Part::Feature] Shape006  label="C44_C_1206_3216Metric_504a53cc2dd0"
  Placement = pos=(190.5,-133.025,0) rot=(0,0,-1;1.5708rad)
  shape: bbox 1.6 x 3.2 x 1.6 mm, 28 faces (baked)
FEATURE [App::Link] R21_C_0402_1005Metric_38c94f1f1ba7_ln_004  label="C18_C_0402_1005Metric_92a1be41be9e"
  LinkPlacement = pos=(189.4,-106.5,0) rot=(0,0,1;0rad)
  LinkedObject = -> Shape
  Placement = pos=(189.4,-106.5,0) rot=(0,0,1;0rad)
FEATURE [App::Link] R21_C_0402_1005Metric_38c94f1f1ba7_ln_005  label="C31_C_0402_1005Metric_578c4d3870ae"
  LinkPlacement = pos=(189,-90,0) rot=(0,0,1;3.14159rad)
  LinkedObject = -> Shape
  Placement = pos=(189,-90,0) rot=(0,0,1;3.14159rad)
FEATURE [App::Link] R19_R_0402_1005Metric_9ca80ee487fc_ln_002  label="R3_R_0402_1005Metric_969b0b0747f2"
  LinkPlacement = pos=(191.3,-80.09,0) rot=(0,0,-1;1.5708rad)
  LinkedObject = -> Shape001
  Placement = pos=(191.3,-80.09,0) rot=(0,0,-1;1.5708rad)
FEATURE [App::Link] R21_C_0402_1005Metric_38c94f1f1ba7_ln_006  label="C29_C_0402_1005Metric_878fa2face33"
  LinkPlacement = pos=(185.6,-86.9,0) rot=(0,0,1;1.5708rad)
  LinkedObject = -> Shape
  Placement = pos=(185.6,-86.9,0) rot=(0,0,1;1.5708rad)
FEATURE [Part::Feature] Shape007  label="U6_QFN-20-1EP_4x4mm_Pitch0.5mm_3f7a39cb167c"
  Placement = pos=(190.975,-103.35,0) rot=(0,0,1;1.5708rad)
  shape: bbox 4 x 4 x 0.77 mm, 134 faces (baked)
FEATURE [App::Link] R19_R_0402_1005Metric_9ca80ee487fc_ln_003  label="R18_R_0402_1005Metric_e9874ca0240e"
  LinkPlacement = pos=(195.4,-53,0) rot=(0,0,1;1.5708rad)
  LinkedObject = -> Shape001
  Placement = pos=(195.4,-53,0) rot=(0,0,1;1.5708rad)
FEATURE [App::Link] R19_R_0402_1005Metric_9ca80ee487fc_ln_004  label="R7_R_0402_1005Metric_0d6ee2aba382"
  LinkPlacement = pos=(196.1,-57,0) rot=(0,0,-1;1.5708rad)
  LinkedObject = -> Shape001
  Placement = pos=(196.1,-57,0) rot=(0,0,-1;1.5708rad)
FEATURE [Part::Feature] Shape008  label="L3_L_0402_1005Metric_7322f57e24a3"
  Placement = pos=(191.1,-99,0) rot=(0,0,1;3.14159rad)
  shape: bbox 1 x 0.5 x 0.5 mm, 28 faces (baked)
FEATURE [App::Link] C42_C_0603_1608Metric_3f0e18eb3bdb_ln_001  label="C26_C_0603_1608Metric_e24a75b1fd6c"
  LinkPlacement = pos=(196.7,-53.6,0) rot=(0,0,-1;1.5708rad)
  LinkedObject = -> Shape003
  Placement = pos=(196.7,-53.6,0) rot=(0,0,-1;1.5708rad)
FEATURE [App::Link] R21_C_0402_1005Metric_38c94f1f1ba7_ln_007  label="C41_C_0402_1005Metric_e05767d0328b"
  LinkPlacement = pos=(196.7,-101.5,0) rot=(0,0,1;1.5708rad)
  LinkedObject = -> Shape
  Placement = pos=(196.7,-101.5,0) rot=(0,0,1;1.5708rad)
FEATURE [App::Link] R19_R_0402_1005Metric_9ca80ee487fc_ln_005  label="R6_R_0402_1005Metric_11a2181a152e"
  LinkPlacement = pos=(195.1,-57,0) rot=(0,0,-1;1.5708rad)
  LinkedObject = -> Shape001
  Placement = pos=(195.1,-57,0) rot=(0,0,-1;1.5708rad)
FEATURE [App::Link] C44_C_1206_3216Metric_504a53cc2dd0_ln_  label="C15_C_1206_3216Metric_4eda32e8580f"
  LinkPlacement = pos=(204.5,-79.3,0) rot=(0,0,1;0rad)
  LinkedObject = -> Shape006
  Placement = pos=(204.5,-79.3,0) rot=(0,0,1;0rad)
FEATURE [App::Link] C44_C_1206_3216Metric_504a53cc2dd0_ln_001  label="C22_C_1206_3216Metric_2920babed859"
  LinkPlacement = pos=(204.4,-81.8,0) rot=(0,0,1;0rad)
  LinkedObject = -> Shape006
  Placement = pos=(204.4,-81.8,0) rot=(0,0,1;0rad)
FEATURE [App::Link] R19_R_0402_1005Metric_9ca80ee487fc_ln_006  label="R23_R_0402_1005Metric_7dfb490c449e"
  LinkPlacement = pos=(184.1,-52.41,0) rot=(0,0,1;1.5708rad)
  LinkedObject = -> Shape001
  Placement = pos=(184.1,-52.41,0) rot=(0,0,1;1.5708rad)
FEATURE [Part::Feature] Shape009  label="D516_LED_0603_1608Metric_23db4c450fc7"
  Placement = pos=(189.1,-126.2,0) rot=(0,0,1;1.5708rad)
  shape: bbox 0.8 x 1.6 x 1.1 mm, 50 faces (baked)
FEATURE [App::Link] R21_C_0402_1005Metric_38c94f1f1ba7_ln_008  label="C16_C_0402_1005Metric_ccc6f5fbae95"
  LinkPlacement = pos=(192.7,-132.7,0) rot=(0,0,1;1.5708rad)
  LinkedObject = -> Shape
  Placement = pos=(192.7,-132.7,0) rot=(0,0,1;1.5708rad)
FEATURE [App::Link] R21_C_0402_1005Metric_38c94f1f1ba7_ln_009  label="C20_C_0402_1005Metric_339430b002f9"
  LinkPlacement = pos=(204.7,-53.1,0) rot=(0,0,1;3.14159rad)
  LinkedObject = -> Shape
  Placement = pos=(204.7,-53.1,0) rot=(0,0,1;3.14159rad)
FEATURE [App::Link] R21_C_0402_1005Metric_38c94f1f1ba7_ln_010  label="C47_C_0402_1005Metric_af42fe187c16"
  LinkPlacement = pos=(195,-99.9,0) rot=(0,0,1;0rad)
  LinkedObject = -> Shape
  Placement = pos=(195,-99.9,0) rot=(0,0,1;0rad)
FEATURE [Part::Feature] Shape010  label="U8_SOT_23_1e3b1a0e5d43"
  Placement = pos=(193.9,-128,0) rot=(0,0,1;3.14159rad)
  shape: bbox 2.5 x 3 x 1.2 mm, 76 faces (baked)
FEATURE [App::Link] R21_C_0402_1005Metric_38c94f1f1ba7_ln_011  label="C6_C_0402_1005Metric_7f7ff18c55e3"
  LinkPlacement = pos=(190.5,-68.8,0) rot=(0,0,1;3.14159rad)
  LinkedObject = -> Shape
  Placement = pos=(190.5,-68.8,0) rot=(0,0,1;3.14159rad)
FEATURE [App::Link] D2_D_SMA_34cf3897dfc1_ln_  label="D1_D_SMA_3cb871b8a290"
  LinkPlacement = pos=(190.3,-109.8,0) rot=(0,0,1;3.14159rad)
  LinkedObject = -> Shape002
  Placement = pos=(190.3,-109.8,0) rot=(0,0,1;3.14159rad)
FEATURE [Part::Feature] Shape011  label="U3_QFN_56_1EP_7x7mm_P04mm_EP32x32mm_92a982e71d8d"
  Placement = pos=(189.6,-74.9,0) rot=(0,0,1;0rad)
  shape: bbox 7 x 7 x 0.95 mm, 350 faces (baked)
FEATURE [App::Link] R21_C_0402_1005Metric_38c94f1f1ba7_ln_012  label="C30_C_0402_1005Metric_cc59a400e17a"
  LinkPlacement = pos=(191,-90,0) rot=(0,0,1;3.14159rad)
  LinkedObject = -> Shape
  Placement = pos=(191,-90,0) rot=(0,0,1;3.14159rad)
FEATURE [App::Link] R21_C_0402_1005Metric_38c94f1f1ba7_ln_013  label="C13_C_0402_1005Metric_d2173120320b"
  LinkPlacement = pos=(198.8,-57.6,0) rot=(0,0,1;3.14159rad)
  LinkedObject = -> Shape
  Placement = pos=(198.8,-57.6,0) rot=(0,0,1;3.14159rad)
FEATURE [App::Link] L3_L_0402_1005Metric_7322f57e24a3_ln_  label="L4_L_0402_1005Metric_e4c50960bfc8"
  LinkPlacement = pos=(190.7,-97.6,0) rot=(0,0,1;0rad)
  LinkedObject = -> Shape008
  Placement = pos=(190.7,-97.6,0) rot=(0,0,1;0rad)
FEATURE [App::Link] R21_C_0402_1005Metric_38c94f1f1ba7_ln_014  label="C2_C_0402_1005Metric_4b4f118f5010"
  LinkPlacement = pos=(185.6,-81.3,0) rot=(0,0,1;3.14159rad)
  LinkedObject = -> Shape
  Placement = pos=(185.6,-81.3,0) rot=(0,0,1;3.14159rad)
FEATURE [App::Link] D516_LED_0603_1608Metric_23db4c450fc7_ln_  label="D517_LED_0603_1608Metric_b24ae36cc63a"
  LinkPlacement = pos=(190.7,-126.2,0) rot=(0,0,1;1.5708rad)
  LinkedObject = -> Shape009
  Placement = pos=(190.7,-126.2,0) rot=(0,0,1;1.5708rad)
FEATURE [App::Link] R21_C_0402_1005Metric_38c94f1f1ba7_ln_015  label="C10_C_0402_1005Metric_25fd1e42a1bf"
  LinkPlacement = pos=(186.1,-69.6,0) rot=(0,0,1;1.5708rad)
  LinkedObject = -> Shape
  Placement = pos=(186.1,-69.6,0) rot=(0,0,1;1.5708rad)
FEATURE [App::Link] R21_C_0402_1005Metric_38c94f1f1ba7_ln_016  label="C33_C_0402_1005Metric_872bb8822931"
  LinkPlacement = pos=(204.2,-51.5,0) rot=(0,0,-1;1.5708rad)
  LinkedObject = -> Shape
  Placement = pos=(204.2,-51.5,0) rot=(0,0,-1;1.5708rad)
FEATURE [App::Link] R21_C_0402_1005Metric_38c94f1f1ba7_ln_017  label="C43_C_0402_1005Metric_b465c88a99c7"
  LinkPlacement = pos=(202.2,-129.1,0) rot=(0,0,-1;1.5708rad)
  LinkedObject = -> Shape
  Placement = pos=(202.2,-129.1,0) rot=(0,0,-1;1.5708rad)
FEATURE [App::Link] R19_R_0402_1005Metric_9ca80ee487fc_ln_007  label="R4_R_0402_1005Metric_18a2017ffd4b"
  LinkPlacement = pos=(194,-57,0) rot=(0,0,-1;1.5708rad)
  LinkedObject = -> Shape001
  Placement = pos=(194,-57,0) rot=(0,0,-1;1.5708rad)
FEATURE [App::Link] C44_C_1206_3216Metric_504a53cc2dd0_ln_002  label="C25_C_1206_3216Metric_a9b05d8d3b1b"
  LinkPlacement = pos=(199.6,-132.5,0) rot=(0,0,1;0rad)
  LinkedObject = -> Shape006
  Placement = pos=(199.6,-132.5,0) rot=(0,0,1;0rad)
FEATURE [Part::Feature] Shape012  label="Y1_Crystal_SMD_3225-4Pin_3.2x2.5mm_5bc66405eca2"
  Placement = pos=(186.9,-83.7,0) rot=(0,0,1;0rad)
  shape: bbox 3.2 x 2.501 x 0.64 mm, 28 faces (baked)
FEATURE [App::Link] R19_R_0402_1005Metric_9ca80ee487fc_ln_008  label="R16_R_0402_1005Metric_1ac23e3eb529"
  LinkPlacement = pos=(205.3,-51.5,0) rot=(0,0,-1;1.5708rad)
  LinkedObject = -> Shape001
  Placement = pos=(205.3,-51.5,0) rot=(0,0,-1;1.5708rad)
FEATURE [App::Link] R19_R_0402_1005Metric_9ca80ee487fc_ln_009  label="Q1_R_0402_1005Metric_19db146f615e"
  LinkPlacement = pos=(204.7,-50,0) rot=(0,0,1;0rad)
  LinkedObject = -> Shape001
  Placement = pos=(204.7,-50,0) rot=(0,0,1;0rad)
FEATURE [App::Link] U8_SOT_23_1e3b1a0e5d43_ln_  label="Q2_SOT_23_816b0a6423d4"
  LinkPlacement = pos=(191.1,-56.8,0) rot=(0,0,1;1.5708rad)
  LinkedObject = -> Shape010
  Placement = pos=(191.1,-56.8,0) rot=(0,0,1;1.5708rad)
FEATURE [App::Link] R21_C_0402_1005Metric_38c94f1f1ba7_ln_018  label="C24_C_0402_1005Metric_c74ed45d8278"
  LinkPlacement = pos=(196.3,-103.1,0) rot=(0,0,1;0rad)
  LinkedObject = -> Shape
  Placement = pos=(196.3,-103.1,0) rot=(0,0,1;0rad)
FEATURE [App::Link] C44_C_1206_3216Metric_504a53cc2dd0_ln_003  label="C35_C_1206_3216Metric_0a151451740c"
  LinkPlacement = pos=(201.1,-105.5,0) rot=(0,0,1;1.5708rad)
  LinkedObject = -> Shape006
  Placement = pos=(201.1,-105.5,0) rot=(0,0,1;1.5708rad)
FEATURE [App::Link] R21_C_0402_1005Metric_38c94f1f1ba7_ln_019  label="R22_C_0402_1005Metric_0e379b04b221"
  LinkPlacement = pos=(195.3,-65,0) rot=(0,0,1;0rad)
  LinkedObject = -> Shape
  Placement = pos=(195.3,-65,0) rot=(0,0,1;0rad)
FEATURE [App::Link] R19_R_0402_1005Metric_9ca80ee487fc_ln_010  label="R17_R_0402_1005Metric_c84f106557fc"
  LinkPlacement = pos=(193.4,-52.99,0) rot=(0,0,1;1.5708rad)
  LinkedObject = -> Shape001
  Placement = pos=(193.4,-52.99,0) rot=(0,0,1;1.5708rad)
FEATURE [App::Link] R21_C_0402_1005Metric_38c94f1f1ba7_ln_020  label="C34_C_0402_1005Metric_69e14d7ecb16"
  LinkPlacement = pos=(200.7,-51.3,0) rot=(0,0,-1;1.5708rad)
  LinkedObject = -> Shape
  Placement = pos=(200.7,-51.3,0) rot=(0,0,-1;1.5708rad)
FEATURE [App::Link] R21_C_0402_1005Metric_38c94f1f1ba7_ln_021  label="C32_C_0402_1005Metric_dab31895c2db"
  LinkPlacement = pos=(187,-90,0) rot=(0,0,1;3.14159rad)
  LinkedObject = -> Shape
  Placement = pos=(187,-90,0) rot=(0,0,1;3.14159rad)
FEATURE [App::Link] R21_C_0402_1005Metric_38c94f1f1ba7_ln_022  label="C23_C_0402_1005Metric_a91c703b8113"
  LinkPlacement = pos=(195,-100.9,0) rot=(0,0,1;3.14159rad)
  LinkedObject = -> Shape
  Placement = pos=(195,-100.9,0) rot=(0,0,1;3.14159rad)
FEATURE [Part::Feature] Shape013  label="J4_PinHeader_2x07_P127mm_Vertical_bf31e59c633b"
  Placement = pos=(194.765,-81.49,0) rot=(0,0,1;0rad)
  shape: bbox 3.4 x 8.89 x 6.3 mm, 298 faces (baked)
FEATURE [App::Link] R21_C_0402_1005Metric_38c94f1f1ba7_ln_023  label="C11_C_0402_1005Metric_ee0f1353bdd2"
  LinkPlacement = pos=(192.4,-68.8,0) rot=(0,0,1;0rad)
  LinkedObject = -> Shape
  Placement = pos=(192.4,-68.8,0) rot=(0,0,1;0rad)
FEATURE [App::Link] R19_R_0402_1005Metric_9ca80ee487fc_ln_011  label="R12_R_0402_1005Metric_1dd42002f4d0"
  LinkPlacement = pos=(200.1,-129.09,0) rot=(0,0,1;1.5708rad)
  LinkedObject = -> Shape001
  Placement = pos=(200.1,-129.09,0) rot=(0,0,1;1.5708rad)
FEATURE [App::Link] R21_C_0402_1005Metric_38c94f1f1ba7_ln_024  label="C27_C_0402_1005Metric_39aa6632ecb3"
  LinkPlacement = pos=(192.72,-97.6,0) rot=(0,0,1;0rad)
  LinkedObject = -> Shape
  Placement = pos=(192.72,-97.6,0) rot=(0,0,1;0rad)
FEATURE [App::Link] R19_R_0402_1005Metric_9ca80ee487fc_ln_012  label="R5_R_0402_1005Metric_a55a78cb6167"
  LinkPlacement = pos=(197.2,-57,0) rot=(0,0,-1;1.5708rad)
  LinkedObject = -> Shape001
  Placement = pos=(197.2,-57,0) rot=(0,0,-1;1.5708rad)
FEATURE [App::Link] R19_R_0402_1005Metric_9ca80ee487fc_ln_013  label="R1_R_0402_1005Metric_f5b816f9472f"
  LinkPlacement = pos=(199.8,-69.2,0) rot=(0,0,1;0rad)
  LinkedObject = -> Shape001
  Placement = pos=(199.8,-69.2,0) rot=(0,0,1;0rad)
FEATURE [App::Link] D516_LED_0603_1608Metric_23db4c450fc7_ln_001  label="D518_LED_0603_1608Metric_9ded9605b13f"
  LinkPlacement = pos=(195.4,-63.5,0) rot=(0,0,1;0rad)
  LinkedObject = -> Shape009
  Placement = pos=(195.4,-63.5,0) rot=(0,0,1;0rad)
FEATURE [App::Link] C44_C_1206_3216Metric_504a53cc2dd0_ln_004  label="C21_C_1206_3216Metric_429a80aec131"
  LinkPlacement = pos=(194.9,-112.9,0) rot=(0,0,1;3.14159rad)
  LinkedObject = -> Shape006
  Placement = pos=(194.9,-112.9,0) rot=(0,0,1;3.14159rad)
FEATURE [Part::Feature] Shape014  label="U9_SOT_23_6_c7a49d86fbfe"
  Placement = pos=(188.6,-87.6,0) rot=(0,0,1;3.14159rad)
  shape: bbox 2.8 x 2.9 x 1.55 mm, 124 faces (baked)
FEATURE [App::Link] R21_C_0402_1005Metric_38c94f1f1ba7_ln_025  label="C17_C_0402_1005Metric_54b876e493f1"
  LinkPlacement = pos=(189.4,-107.5,0) rot=(0,0,1;0rad)
  LinkedObject = -> Shape
  Placement = pos=(189.4,-107.5,0) rot=(0,0,1;0rad)
FEATURE [Part::Feature] Shape015  label="SW1_SW_SPST_PTS645_03fdbfd9ae36"
  Placement = pos=(200.6,-63,0) rot=(0,0,-1;1.5708rad)
  shape: bbox 6 x 9 x 4.3 mm, 97 faces (baked)
FEATURE [App::Link] R19_R_0402_1005Metric_9ca80ee487fc_ln_014  label="R24_R_0402_1005Metric_04ceae6545c3"
  LinkPlacement = pos=(188.2,-57.7,0) rot=(0,0,-1;1.5708rad)
  LinkedObject = -> Shape001
  Placement = pos=(188.2,-57.7,0) rot=(0,0,-1;1.5708rad)
FEATURE [App::Link] Y1_Crystal_SMD_3225_4Pin_3_2x2_5mm_5bc66405eca2_ln_  label="Y2_Crystal_SMD_3225-4Pin_3.2x2.5mm_c0e7deee875b"
  LinkPlacement = pos=(195.8,-105.9,0) rot=(0,0,1;1.5708rad)
  LinkedObject = -> Shape012
  Placement = pos=(195.8,-105.9,0) rot=(0,0,1;1.5708rad)
FEATURE [App::Link] R19_R_0402_1005Metric_9ca80ee487fc_ln_015  label="R10_R_0402_1005Metric_299a858bebda"
  LinkPlacement = pos=(195.5,-77.1,0) rot=(0,0,1;1.5708rad)
  LinkedObject = -> Shape001
  Placement = pos=(195.5,-77.1,0) rot=(0,0,1;1.5708rad)
FEATURE [App::Link] R19_R_0402_1005Metric_9ca80ee487fc_ln_016  label="R9_R_0402_1005Metric_84cfa7eb0e8e"
  LinkPlacement = pos=(198.9,-129.1,0) rot=(0,0,-1;1.5708rad)
  LinkedObject = -> Shape001
  Placement = pos=(198.9,-129.1,0) rot=(0,0,-1;1.5708rad)
FEATURE [App::Link] R21_C_0402_1005Metric_38c94f1f1ba7_ln_026  label="C28_C_0402_1005Metric_fdbb3c7674a5"
  LinkPlacement = pos=(194.2,-98.1,0) rot=(0,0,1;1.5708rad)
  LinkedObject = -> Shape
  Placement = pos=(194.2,-98.1,0) rot=(0,0,1;1.5708rad)
FEATURE [App::Link] R19_R_0402_1005Metric_9ca80ee487fc_ln_017  label="R11_R_0402_1005Metric_60fb483f3fd5"
  LinkPlacement = pos=(196.7,-77.1,0) rot=(0,0,-1;1.5708rad)
  LinkedObject = -> Shape001
  Placement = pos=(196.7,-77.1,0) rot=(0,0,-1;1.5708rad)
FEATURE [App::Link] R21_C_0402_1005Metric_38c94f1f1ba7_ln_027  label="C4_C_0402_1005Metric_564747b89293"
  LinkPlacement = pos=(187.92,-81.4,0) rot=(0,0,1;0rad)
  LinkedObject = -> Shape
  Placement = pos=(187.92,-81.4,0) rot=(0,0,1;0rad)
FEATURE [Part::Feature] Shape016  label="L1_Sf㱟fd_sp_e828286b0ac3"
  Placement = pos=(200.4,-114.7,0) rot=(0,0,1;1.5708rad)
  shape: bbox 7.058 x 7.058 x 2.5 mm, 79 faces (baked)
FEATURE [App::Link] L3_L_0402_1005Metric_7322f57e24a3_ln_001  label="L2_L_0402_1005Metric_cbc56b11f79b"
  LinkPlacement = pos=(192,-100.1,0) rot=(0,0,1;3.14159rad)
  LinkedObject = -> Shape008
  Placement = pos=(192,-100.1,0) rot=(0,0,1;3.14159rad)
FEATURE [App::Link] R19_R_0402_1005Metric_9ca80ee487fc_ln_018  label="R8_R_0402_1005Metric_044c423f79ff"
  LinkPlacement = pos=(197.8,-129.1,0) rot=(0,0,1;1.5708rad)
  LinkedObject = -> Shape001
  Placement = pos=(197.8,-129.1,0) rot=(0,0,1;1.5708rad)
FEATURE [App::Link] R21_C_0402_1005Metric_38c94f1f1ba7_ln_028  label="C5_C_0402_1005Metric_ff954b7ecdeb"
  LinkPlacement = pos=(190.5,-69.9,0) rot=(0,0,1;3.14159rad)
  LinkedObject = -> Shape
  Placement = pos=(190.5,-69.9,0) rot=(0,0,1;3.14159rad)
FEATURE [App::Link] R19_R_0402_1005Metric_9ca80ee487fc_ln_019  label="R14_R_0402_1005Metric_07a2d9395c6f"
  LinkPlacement = pos=(206.4,-51.5,0) rot=(0,0,-1;1.5708rad)
  LinkedObject = -> Shape001
  Placement = pos=(206.4,-51.5,0) rot=(0,0,-1;1.5708rad)
FEATURE [App::Link] R19_R_0402_1005Metric_9ca80ee487fc_ln_020  label="R13_R_0402_1005Metric_6ddea6fc7991"
  LinkPlacement = pos=(201.1,-129.1,0) rot=(0,0,-1;1.5708rad)
  LinkedObject = -> Shape001
  Placement = pos=(201.1,-129.1,0) rot=(0,0,-1;1.5708rad)
FEATURE [App::Part] Top_931
  Group = -> [Shape,R21_C_0402_1005Metric_38c94f1f1ba7_ln_,R21_C_0402_1005Metric_38c94f1f1ba7_ln_001,Shape001,R21_C_0402_1005Metric_38c94f1f1ba7_ln_002,Shape002,Shape003,Shape004,Shape005,R19_R_0402_1005Metric_9ca80ee487fc_ln_,C42_C_0603_1608Metric_3f0e18eb3bdb_ln_,R21_C_0402_1005Metric_38c94f1f1ba7_ln_003,R19_R_0402_1005Metric_9ca80ee487fc_ln_001,Shape006,R21_C_0402_1005Metric_38c94f1f1ba7_ln_004,+66 more]
  Origin = -> Origin003
FEATURE [Part::Feature] Shape017  label="BT1_MPD_BH_18650_PC2_17c3f7ae5d37"
  Placement = pos=(195.3,-132,-1.6) rot=(0.707107,0.707107,0;3.14159rad)
  shape: bbox 20.9 x 77.7 x 22.2 mm, 62 faces (baked)
FEATURE [Part::Feature] Shape018  label="J1_USB_Mini-B_Lumberg_2486_01_Horizontal_f06c414dff7d"
  Placement = pos=(195.3,-50.6,-1.6) rot=(1,0,0;3.14159rad)
  shape: bbox 9.9 x 9.2 x 4.997 mm, 472 faces (baked)
FEATURE [App::Part] Bot_931
  Group = -> [Shape017,Shape018]
  Origin = -> Origin004
FEATURE [App::Part] Step_Models_931
  Group = -> [Top_931,Bot_931]
  Origin = -> Origin002
FEATURE [App::Part] Board_931  label="ButterflyBadge"
  Group = -> [Local_CS_931,Board_Geoms_931,Step_Models_931]
  Origin = -> Origin001
